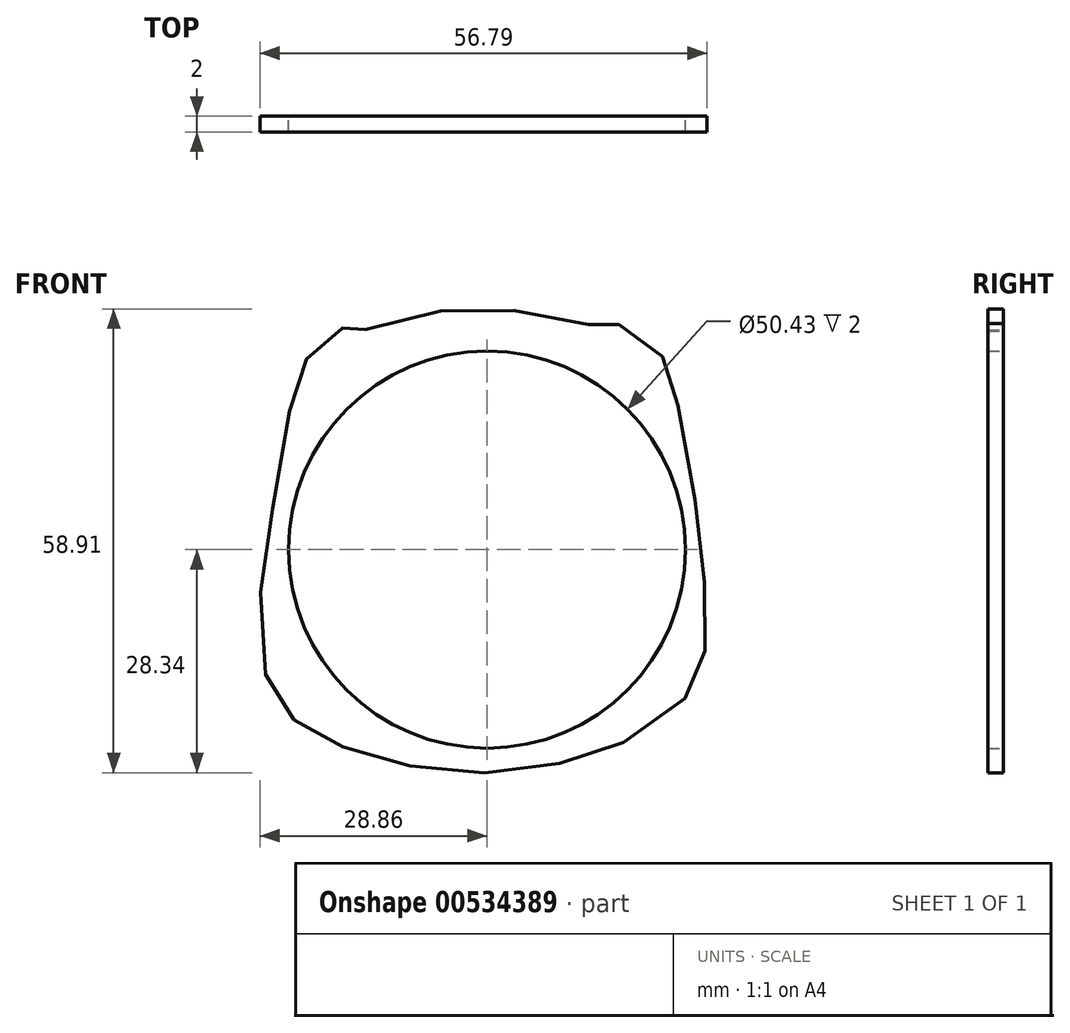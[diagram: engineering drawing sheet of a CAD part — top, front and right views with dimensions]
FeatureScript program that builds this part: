
annotation { "Feature Type Name" : "Feature", "Feature Type Description" : "" }
export const myFeature = defineFeature(function(context is Context, id is Id, definition is map)
    precondition{}
    {
        {
            var Q0;
            Q0=qCreatedBy(makeId("Front.planeOp"),FACE);
            var sketch = newSketch(context, id + "F0", { "sketchPlane" : qUnion([Q0])});
            skFitSpline(sketch, "E0", {"points": [v(-15.43, 27.94) * mm, v(-8.18, 29.9) * mm, v(-0.1, 30.53) * mm, v(6.96, 29.95) * mm, v(13.75, 28.23) * mm, v(15.02, 27.83) * mm, v(16.05, 28.69) * mm, v(17.38, 28.29) * mm, v(21, 25.93) * mm, v(23.2, 22.93) * mm, v(23.77, 20.75) * mm, v(25.84, 9.87) * mm, v(27.16, 0.31) * mm, v(27.91, -8.6) * mm, v(27.57, -13.44) * mm, v(26.24, -17.07) * mm, v(24.28, -19.89) * mm, v(17.1, -24.6) * mm, v(11.8, -26.5) * mm, v(4.31, -28) * mm, v(-3, -28.3) * mm, v(-10.48, -27.37) * mm, v(-16.87, -25.64) * mm, v(-21.64, -23.51) * mm, v(-24.64, -21.5) * mm, v(-27.11, -18.16) * mm, v(-28.43, -14.65) * mm, v(-28.72, -4.46) * mm, v(-27.34, 4.75) * mm, v(-25.1, 17.75) * mm, v(-23.48, 23.67) * mm, v(-23.14, 24.02) * mm, v(-21.53, 25.92) * mm, v(-18.82, 27.93) * mm, v(-17.32, 28.68) * mm, v(-16.98, 28.8) * mm, v(-16.17, 28.45) * mm, v(-15.43, 27.94) * mm]});
            skCircle(sketch, "E1", {"center": v(0, 0) * mm, "radius": 25.22 * mm});
            skCircle(sketch, "E2.0", {"center": v(0, 0) * mm, "radius": 26.22 * mm});
            skSolve(sketch);
        }
        {
            var Q0;
            Q0=qCreatedBy(makeId("Front.planeOp"),FACE);
            cPlane(context, id + "F1", {"entities" : qUnion([Q0]), "cplaneType" : CPlaneType.OFFSET, "offset" : 20 * mm, "oppositeDirection" : true, "width" : 152.4 * mm, "height" : 152.4 * mm});
        }
        {
            var Q0;
            Q0=makeQuery(id+"F0.imprint","IMPRINT",FACE,{"disambiguationData":[TD([[makeQuery(id+"F0.imprint","IMPRINT",EDGE,{"derivedFrom":sQuery(id+"F0.wireOp",EDGE,"E0")}),-1.0]])]});
            var Q1;
            Q1=makeQuery(id+"F0.imprint","IMPRINT",FACE,{"disambiguationData":[TD([[makeQuery(id+"F0.imprint","IMPRINT",EDGE,{"derivedFrom":sQuery(id+"F0.wireOp",EDGE,"E1")}),-1.0]])]});
            extrude(context, id + "F2", {"entities" : qUnion([Q0, Q1]), "depth" : 2 * mm, "offsetDistance" : 25.4 * mm});
        }
    });
